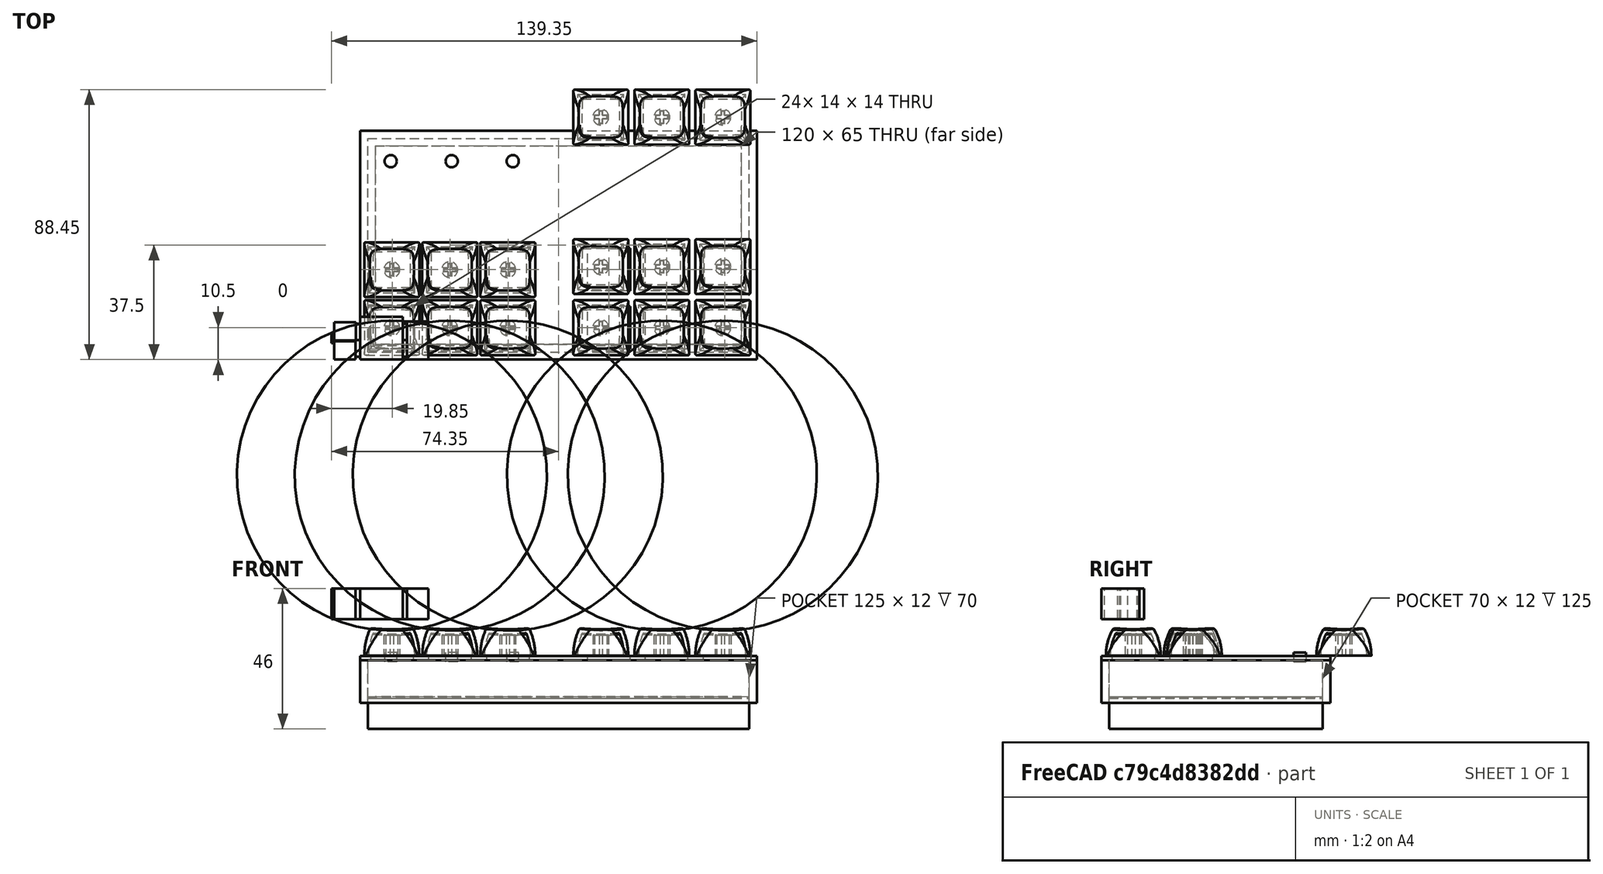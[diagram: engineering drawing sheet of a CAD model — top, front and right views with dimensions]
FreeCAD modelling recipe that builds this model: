
FCSTD DOCUMENT  (FreeCAD 1.0R39109 (Git))
Label: control-v0.4
License: All rights reserved
LicenseURL: https://en.wikipedia.org/wiki/All_rights_reserved
objects: Part::Box×28, Part::Feature×15, Part::Cut×15, App::DocumentObjectGroup×4, Part::Cylinder×3, Part::FeaturePython×1
note: 62 computed .brp shape members not serialized (recipe doc carries the construction recipe); baked Part::Feature solids carry a one-line shape summary decoded from their .brp

FEATURE [Part::Box] Box  label="Upper Housing"
  AttacherType = Attacher::AttachEngine3D
  Height = 1.35
  Length = 130
  Placement = pos=(0,0,11.5) rot=(0,0,1;0rad)
  Width = 75
FEATURE [Part::Box] Box001  label="Cube"
  AttacherType = Attacher::AttachEngine3D
  Height = 4
  Length = 14
  Placement = pos=(3.5,3.5,10) rot=(0,0,1;0rad)
  Width = 14
FEATURE [Part::Box] Box002  label="Cube001"
  AttacherType = Attacher::AttachEngine3D
  Height = 4
  Length = 14
  Placement = pos=(3.5,22.5,10) rot=(0,0,1;0rad)
  Width = 14
FEATURE [Part::Box] Box003  label="Cube002"
  AttacherType = Attacher::AttachEngine3D
  Height = 4
  Length = 14
  Placement = pos=(22.5,22.5,10) rot=(0,0,1;0rad)
  Width = 14
FEATURE [Part::Box] Box005  label="Cube004"
  AttacherType = Attacher::AttachEngine3D
  Height = 4
  Length = 14
  Placement = pos=(41.5,3.5,10) rot=(0,0,1;0rad)
  Width = 14
FEATURE [Part::Box] Box006  label="Cube005"
  AttacherType = Attacher::AttachEngine3D
  Height = 4
  Length = 14
  Placement = pos=(41.5,22.5,10) rot=(0,0,1;0rad)
  Width = 14
FEATURE [Part::Box] Box007  label="Cube006"
  AttacherType = Attacher::AttachEngine3D
  Height = 4
  Length = 14
  Placement = pos=(112.5,3.5,10) rot=(0,0,1;0rad)
  Width = 14
FEATURE [Part::Box] Box008  label="Cube007"
  AttacherType = Attacher::AttachEngine3D
  Height = 4
  Length = 14
  Placement = pos=(93.5,3.5,10) rot=(0,0,1;0rad)
  Width = 14
FEATURE [Part::Box] Box009  label="Cube008"
  AttacherType = Attacher::AttachEngine3D
  Height = 4
  Length = 14
  Placement = pos=(74.5,3.5,10) rot=(0,0,1;0rad)
  Width = 14
FEATURE [Part::Box] Box010  label="Cube009"
  AttacherType = Attacher::AttachEngine3D
  Height = 4
  Length = 14
  Placement = pos=(74.5,22.5,10) rot=(0,0,1;0rad)
  Width = 14
FEATURE [Part::Box] Box011  label="Cube010"
  AttacherType = Attacher::AttachEngine3D
  Height = 4
  Length = 14
  Placement = pos=(93.5,22.5,10) rot=(0,0,1;0rad)
  Width = 14
FEATURE [Part::Box] Box012  label="Cube011"
  AttacherType = Attacher::AttachEngine3D
  Height = 4
  Length = 14
  Placement = pos=(112.5,22.5,10) rot=(0,0,1;0rad)
  Width = 14
FEATURE [Part::Cylinder] Cylinder
  Angle = 360
  AttacherType = Attacher::AttachEngine3D
  FirstAngle = 0
  Height = 3
  Placement = pos=(10,65,11) rot=(0,0,1;0rad)
  Radius = 2
  SecondAngle = 0
FEATURE [Part::Cylinder] Cylinder001
  Angle = 360
  AttacherType = Attacher::AttachEngine3D
  FirstAngle = 0
  Height = 3
  Placement = pos=(30,65,11) rot=(0,0,1;0rad)
  Radius = 2
  SecondAngle = 0
FEATURE [Part::Cylinder] Cylinder002
  Angle = 360
  AttacherType = Attacher::AttachEngine3D
  FirstAngle = 0
  Height = 3
  Placement = pos=(50,65,11) rot=(0,0,1;0rad)
  Radius = 2
  SecondAngle = 0
FEATURE [App::DocumentObjectGroup] Group003  label="Rotories"
  Group = -> [Cylinder,Cylinder001,Cylinder002]
FEATURE [Part::Feature] Part__Feature  label="1u v2"
  Placement = pos=(21.5,15,13) rot=(1,0,0;1.5708rad)
  shape: bbox 18 x 18.01 x 11.79 mm, 51 faces (baked)
FEATURE [Part::Box] Box004  label="Cube003"
  AttacherType = Attacher::AttachEngine3D
  Height = 4
  Length = 14
  Placement = pos=(22.5,3.5,10) rot=(0,0,1;0rad)
  Width = 14
FEATURE [Part::Feature] Part__Feature001  label="1u v003"
  Placement = pos=(40.5,15,13) rot=(1,0,0;1.5708rad)
  shape: bbox 18 x 18.01 x 11.79 mm, 51 faces (baked)
FEATURE [Part::Feature] Part__Feature002  label="1u v004"
  Placement = pos=(59.5,15,13) rot=(1,0,0;1.5708rad)
  shape: bbox 18 x 18.01 x 11.79 mm, 51 faces (baked)
FEATURE [Part::Feature] Part__Feature003  label="1u v005"
  Placement = pos=(59.5,34,13) rot=(1,0,0;1.5708rad)
  shape: bbox 18 x 18.01 x 11.79 mm, 51 faces (baked)
FEATURE [Part::Feature] Part__Feature004  label="1u v006"
  Placement = pos=(21.5,34,13) rot=(1,0,0;1.5708rad)
  shape: bbox 18 x 18.01 x 11.79 mm, 51 faces (baked)
FEATURE [Part::Feature] Part__Feature005  label="1u v007"
  Placement = pos=(40.5,34,13) rot=(1,0,0;1.5708rad)
  shape: bbox 18 x 18.01 x 11.79 mm, 51 faces (baked)
FEATURE [Part::Feature] Part__Feature006  label="1u v008"
  Placement = pos=(90,35,13) rot=(1,0,0;1.5708rad)
  shape: bbox 18 x 18.01 x 11.79 mm, 51 faces (baked)
FEATURE [Part::Feature] Part__Feature007  label="1u v009"
  Placement = pos=(90,15,13) rot=(1,0,0;1.5708rad)
  shape: bbox 18 x 18.01 x 11.79 mm, 51 faces (baked)
FEATURE [Part::Feature] Part__Feature008  label="1u v010"
  Placement = pos=(110,15,13) rot=(1,0,0;1.5708rad)
  shape: bbox 18 x 18.01 x 11.79 mm, 51 faces (baked)
FEATURE [Part::Feature] Part__Feature009  label="1u v011"
  Placement = pos=(110,35,13) rot=(1,0,0;1.5708rad)
  shape: bbox 18 x 18.01 x 11.79 mm, 51 faces (baked)
FEATURE [Part::Feature] Part__Feature010  label="1u v012"
  Placement = pos=(130,15,13) rot=(1,0,0;1.5708rad)
  shape: bbox 18 x 18.01 x 11.79 mm, 51 faces (baked)
FEATURE [Part::Feature] Part__Feature011  label="1u v013"
  Placement = pos=(130,35,13) rot=(1,0,0;1.5708rad)
  shape: bbox 18 x 18.01 x 11.79 mm, 51 faces (baked)
FEATURE [Part::Feature] Part__Feature012  label="1u v014"
  Placement = pos=(130,84,13) rot=(1,0,0;1.5708rad)
  shape: bbox 18 x 18.01 x 11.79 mm, 51 faces (baked)
FEATURE [Part::Feature] Part__Feature013  label="1u v015"
  Placement = pos=(110,84,13) rot=(1,0,0;1.5708rad)
  shape: bbox 18 x 18.01 x 11.79 mm, 51 faces (baked)
FEATURE [Part::Feature] Part__Feature014  label="1u v016"
  Placement = pos=(90,84,13) rot=(1,0,0;1.5708rad)
  shape: bbox 18 x 18.01 x 11.79 mm, 51 faces (baked)
FEATURE [App::DocumentObjectGroup] Group004  label="Keycaps"
  Group = -> [Part__Feature,Part__Feature001,Part__Feature002,Part__Feature004,Part__Feature005,Part__Feature003,Part__Feature007,Part__Feature008,Part__Feature010,Part__Feature006,Part__Feature009,Part__Feature011,Part__Feature012,Part__Feature013,Part__Feature014]
FEATURE [Part::Cut] Cut
  Base = -> Box
  Tool = -> Box001
FEATURE [Part::Cut] Cut001
  Base = -> Cut
  Tool = -> Box004
FEATURE [Part::Cut] Cut002
  Base = -> Cut001
  Tool = -> Box005
FEATURE [Part::Cut] Cut003
  Base = -> Cut002
  Tool = -> Box002
FEATURE [Part::Cut] Cut004
  Base = -> Cut003
  Tool = -> Box003
FEATURE [Part::Cut] Cut005
  Base = -> Cut004
  Tool = -> Box006
FEATURE [Part::Cut] Cut006
  Base = -> Cut005
  Tool = -> Box009
FEATURE [Part::Cut] Cut007
  Base = -> Cut006
  Tool = -> Box008
FEATURE [Part::Cut] Cut008
  Base = -> Cut007
  Tool = -> Box007
FEATURE [Part::Cut] Cut009
  Base = -> Cut008
  Tool = -> Box010
FEATURE [Part::Cut] Cut010
  Base = -> Cut009
  Tool = -> Box011
FEATURE [Part::Cut] Cut011
  Base = -> Cut010
  Tool = -> Box012
FEATURE [App::DocumentObjectGroup] Group001  label="Upper Housing2"
  Group = -> [Cut011]
FEATURE [Part::Box] Box016  label="Cube015"
  AttacherType = Attacher::AttachEngine3D
  Height = 15
  Length = 130
  Placement = pos=(0,0,-13.5) rot=(0,0,1;0rad)
  Width = 75
FEATURE [Part::Box] Box017  label="Cube016"
  AttacherType = Attacher::AttachEngine3D
  Height = 17.5
  Length = 125
  Placement = pos=(2.5,2.5,-11.5) rot=(0,0,1;0rad)
  Width = 70
FEATURE [Part::Box] Box018  label="Cube017"
  AttacherType = Attacher::AttachEngine3D
  Height = 10
  Length = 125
  Placement = pos=(2.5,2.5,-11) rot=(0,0,1;0rad)
  Width = 70
FEATURE [Part::Cut] Cut012
  Base = -> Box016
  Placement = pos=(0,0,11) rot=(0,0,1;0rad)
  Tool = -> Box017
FEATURE [Part::Box] Box019  label="Cube018"
  AttacherType = Attacher::AttachEngine3D
  Height = 10
  Length = 14
  Placement = pos=(0,0,25) rot=(0,0,1;0rad)
  Width = 14
FEATURE [Part::Box] Box020  label="Cube019"
  AttacherType = Attacher::AttachEngine3D
  Height = 10
  Length = 1.35
  Placement = pos=(14,6.35,25) rot=(0,0,1;0rad)
  Width = 5.35
FEATURE [Part::Box] Box021  label="Cube020"
  AttacherType = Attacher::AttachEngine3D
  Height = 10
  Length = 1.4
  Placement = pos=(14,1,25) rot=(0,0,1;0rad)
  Width = 5.35
FEATURE [Part::Box] Box022  label="Cube021"
  AttacherType = Attacher::AttachEngine3D
  Height = 10
  Length = 1.45
  Placement = pos=(-1.45,6.35,25) rot=(0,0,1;0rad)
  Width = 5.35
FEATURE [Part::Box] Box023  label="Cube022"
  AttacherType = Attacher::AttachEngine3D
  Height = 10
  Length = 1.5
  Placement = pos=(-1.5,1,25) rot=(0,0,1;0rad)
  Width = 5.35
FEATURE [Part::Box] Box024  label="Cube023"
  AttacherType = Attacher::AttachEngine3D
  Height = 10
  Length = 7
  Placement = pos=(-8.45,6,25) rot=(0,0,1;0rad)
  Width = 6.22
FEATURE [Part::Box] Box025  label="Cube024"
  AttacherType = Attacher::AttachEngine3D
  Height = 10
  Length = 0.9
  Placement = pos=(-9.35,5.35,25) rot=(0,0,1;0rad)
  Width = 3.3
FEATURE [Part::Box] Box026  label="Cube025"
  AttacherType = Attacher::AttachEngine3D
  Height = 10
  Length = 7
  Placement = pos=(15.4,0,25) rot=(0,0,1;0rad)
  Width = 12.45
FEATURE [Part::Box] Box027  label="Cube026"
  AttacherType = Attacher::AttachEngine3D
  Height = 10
  Length = 7
  Placement = pos=(-8.5,0,25) rot=(0,0,1;0rad)
  Width = 6.22
FEATURE [App::DocumentObjectGroup] Group  label="Stab"
  Group = -> [Box019,Box022,Box021,Box023,Box024,Box027,Box025,Box026,Box020]
FEATURE [Part::Box] Box028  label="Cube027"
  AttacherType = Attacher::AttachEngine3D
  Height = 10
  Length = 125
  Placement = pos=(2.5,2.5,-11) rot=(0,0,1;0rad)
  Width = 70
FEATURE [Part::Box] Box029  label="Cube028"
  AttacherType = Attacher::AttachEngine3D
  Height = 14
  Length = 120
  Placement = pos=(5,5,-2.5) rot=(0,0,1;0rad)
  Width = 65
FEATURE [Part::Cut] Cut013
  Base = -> Cut012
  Tool = -> Box029
FEATURE [Part::Box] Box030  label="Lower Housing"
  AttacherType = Attacher::AttachEngine3D
  Height = 2
  Length = 125
  Placement = pos=(2.5,2.5,-2.5) rot=(0,0,1;0rad)
  Width = 70
FEATURE [Part::Cut] Cut014
  Base = -> Cut013
  Tool = -> Box028
FEATURE [Part::FeaturePython] Connect  label="Upper Housing003"  # WARN: FeaturePython — macro-defined, semantics opaque (R4)
  Objects = -> [Group001,Cut014]
  Tolerance = 0
